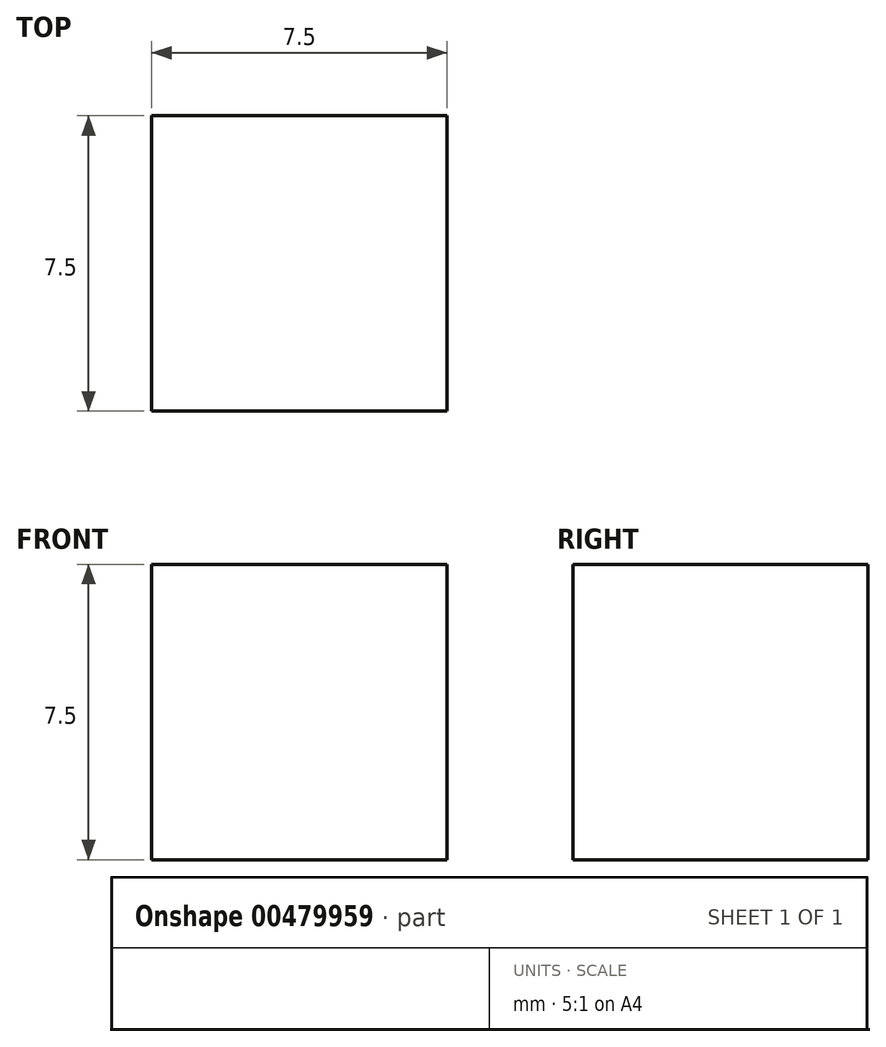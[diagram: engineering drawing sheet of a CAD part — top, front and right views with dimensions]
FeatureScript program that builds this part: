
annotation { "Feature Type Name" : "Feature", "Feature Type Description" : "" }
export const myFeature = defineFeature(function(context is Context, id is Id, definition is map)
    precondition{}
    {
        {
            var Q0;
            Q0=qCreatedBy(makeId("Front.planeOp"),FACE);
            var sketch = newSketch(context, id + "F0", { "sketchPlane" : qUnion([Q0])});
            skLineSegment(sketch, "E0.bottom", {"start": v(3.75, -3.75) * mm, "end": v(-3.75, -3.75) * mm});
            skLineSegment(sketch, "E0.top", {"start": v(3.75, 3.75) * mm, "end": v(-3.75, 3.75) * mm});
            skLineSegment(sketch, "E0.left", {"start": v(3.75, -3.75) * mm, "end": v(3.75, 3.75) * mm});
            skLineSegment(sketch, "E0.right", {"start": v(-3.75, -3.75) * mm, "end": v(-3.75, 3.75) * mm});
            skPoint(sketch, "E0.middle", {"position": v(0, 0) * mm});
            skSolve(sketch);
        }
        {
            var Q0;
            Q0=makeQuery(id+"F0.imprint","IMPRINT",FACE,{"disambiguationData":[TD([[makeQuery(id+"F0.imprint","IMPRINT",EDGE,{"derivedFrom":sQuery(id+"F0.wireOp",EDGE,"E0.bottom")}),-1.0]])]});
            extrude(context, id + "F1", {"entities" : qUnion([Q0]), "depth" : 7.5 * mm});
        }
    });
